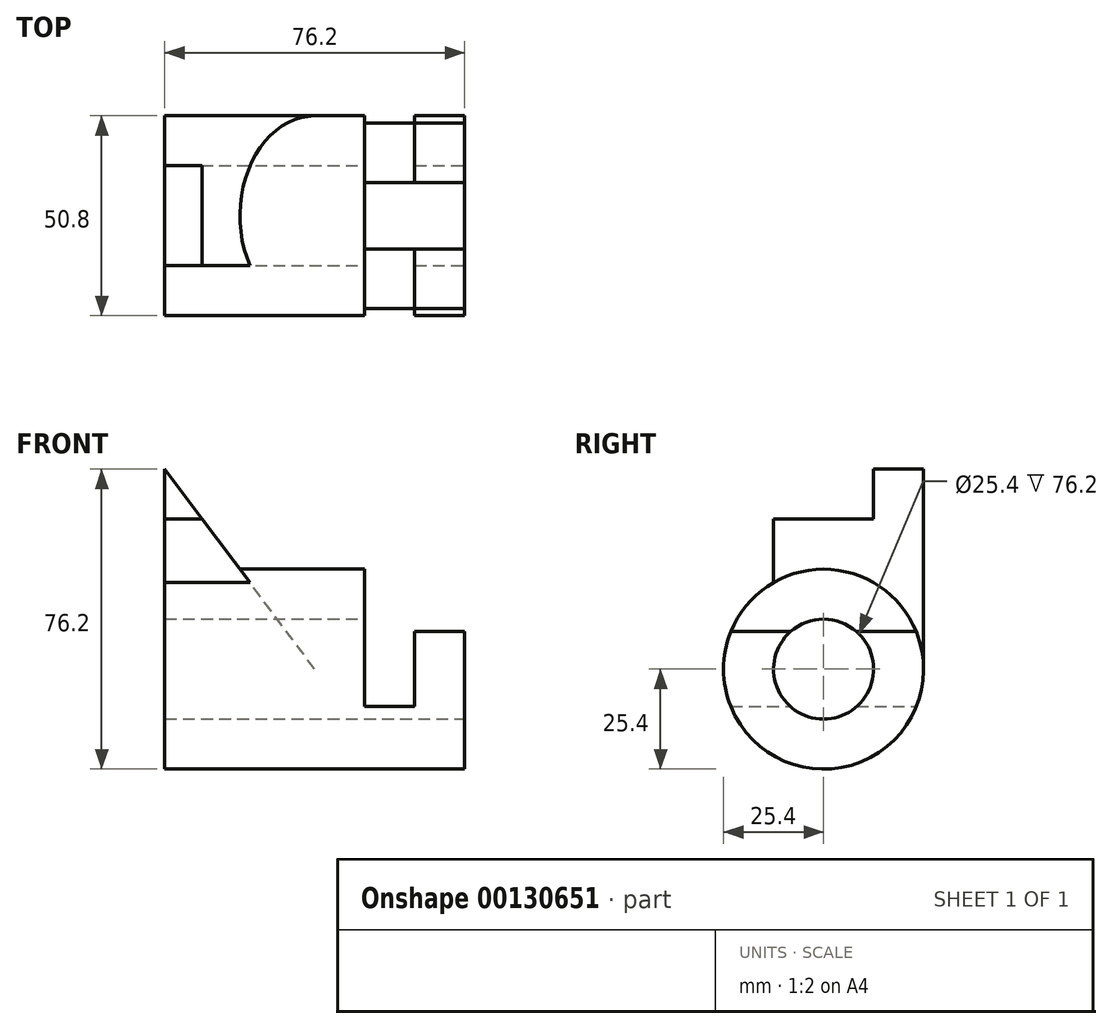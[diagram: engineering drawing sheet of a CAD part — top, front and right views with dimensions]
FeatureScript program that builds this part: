
annotation { "Feature Type Name" : "Feature", "Feature Type Description" : "" }
export const myFeature = defineFeature(function(context is Context, id is Id, definition is map)
    precondition{}
    {
        {
            var Q0;
            Q0=qCreatedBy(makeId("Front.planeOp"),FACE);
            var sketch = newSketch(context, id + "F0", { "sketchPlane" : qUnion([Q0])});
            skLineSegment(sketch, "E0", {"start": v(0, 0) * mm, "end": v(76.2, 0) * mm});
            skLineSegment(sketch, "E1", {"start": v(76.2, 0) * mm, "end": v(76.2, 34.93) * mm});
            skLineSegment(sketch, "E2", {"start": v(76.2, 34.93) * mm, "end": v(63.5, 34.93) * mm});
            skLineSegment(sketch, "E3", {"start": v(63.5, 34.93) * mm, "end": v(63.5, 15.88) * mm});
            skLineSegment(sketch, "E4", {"start": v(63.5, 15.88) * mm, "end": v(50.8, 15.88) * mm});
            skLineSegment(sketch, "E5", {"start": v(50.8, 15.88) * mm, "end": v(50.8, 50.8) * mm});
            skLineSegment(sketch, "E6", {"start": v(50.8, 50.8) * mm, "end": v(19.05, 50.8) * mm});
            skLineSegment(sketch, "E7", {"start": v(19.05, 50.8) * mm, "end": v(0, 76.2) * mm});
            skLineSegment(sketch, "E8", {"start": v(0, 76.2) * mm, "end": v(0, 0) * mm});
            skLineSegment(sketch, "E9", {"start": v(19.05, 50.8) * mm, "end": v(21.43, 47.62) * mm});
            skLineSegment(sketch, "E10", {"start": v(21.43, 47.62) * mm, "end": v(0, 47.62) * mm});
            skLineSegment(sketch, "E11", {"start": v(0, 47.62) * mm, "end": v(0, 76.2) * mm});
            skSolve(sketch);
        }
        {
            var Q0;
            Q0=makeQuery(id+"F0.imprint","IMPRINT",FACE,{"disambiguationData":[TD([[makeQuery(id+"F0.imprint","IMPRINT",EDGE,{"derivedFrom":sQuery(id+"F0.wireOp",EDGE,"E0")}),1.0]])]});
            var Q1;
            Q1=makeQuery(id+"F0.imprint","IMPRINT",FACE,{"disambiguationData":[TD([[makeQuery(id+"F0.imprint","IMPRINT",EDGE,{"derivedFrom":sQuery(id+"F0.wireOp",EDGE,"E7")}),1.0]])]});
            extrude(context, id + "F1", {"entities" : qUnion([Q0, Q1]), "endBound" : BoundingType.SYMMETRIC, "depth" : 50.8 * mm});
        }
        {
            var Q0;
            Q0=makeQuery(id+"F1.opExtrude","SWEPT_FACE",FACE,{"disambiguationData":[OSD([sQuery(id+"F0.wireOp",EDGE,"E1")])]});
            var sketch = newSketch(context, id + "F2", { "sketchPlane" : qUnion([Q0])});
            skCircle(sketch, "E12", {"center": v(0, 25.4) * mm, "radius": 25.4 * mm});
            skSolve(sketch);
        }
        {
            var Q0;
            {var subQ0=sQuery(id+"F2.wireOp",EDGE,"E12");var subQ1=sQuery(id+"F0.wireOp",EDGE,"E1");var subQ2=makeQuery(id+"F1.opExtrude","CAP_EDGE",EDGE,{"disambiguationData":[OSD([subQ1])],"isStart":false});var subQ3=makeQuery(id+"F2.imprint","INTERSECT",VERTEX,{"derivedFrom":[subQ2,subQ0]});Q0=makeQuery(id+"F2.imprint","IMPRINT",FACE,{"disambiguationData":[TD([[makeQuery(id+"F2.imprint","IMPRINT",EDGE,{"disambiguationData":[TD([[subQ3,-1.0]])],"derivedFrom":subQ0}),-1.0]])]});}
            var Q1;
            {var subQ0=sQuery(id+"F2.wireOp",EDGE,"E12");var subQ1=sQuery(id+"F0.wireOp",EDGE,"E1");var subQ2=makeQuery(id+"F1.opExtrude","CAP_EDGE",EDGE,{"disambiguationData":[OSD([subQ1])],"isStart":true});var subQ3=makeQuery(id+"F2.imprint","INTERSECT",VERTEX,{"derivedFrom":[subQ2,subQ0]});Q1=makeQuery(id+"F2.imprint","IMPRINT",FACE,{"disambiguationData":[TD([[makeQuery(id+"F2.imprint","IMPRINT",EDGE,{"disambiguationData":[TD([[subQ3,1.0]])],"derivedFrom":subQ0}),-1.0]])]});}
            extrude(context, id + "F3", {"entities" : qUnion([Q0, Q1]), "operationType" : NewBodyOperationType.REMOVE, "endBound" : BoundingType.THROUGH_ALL, "oppositeDirection" : true, "depth" : 25.4 * mm});
        }
        {
            var Q0;
            Q0=qCreatedBy(makeId("Right.planeOp"),FACE);
            var sketch = newSketch(context, id + "F4", { "sketchPlane" : qUnion([Q0])});
            skLineSegment(sketch, "E13", {"start": v(12.7, 76.2) * mm, "end": v(12.7, 63.5) * mm});
            skLineSegment(sketch, "E14", {"start": v(12.7, 63.5) * mm, "end": v(-12.7, 63.5) * mm});
            skLineSegment(sketch, "E15", {"start": v(-12.7, 63.5) * mm, "end": v(-12.7, 47.4) * mm});
            skArc(sketch, "E16", {"start": v(-12.7, 47.4) * mm, "mid": v(-22, 38.1) * mm, "end": v(-25.4, 25.4) * mm});
            skLineSegment(sketch, "E17", {"start": v(-25.4, 25.4) * mm, "end": v(-25.4, 76.2) * mm});
            skLineSegment(sketch, "E18", {"start": v(-25.4, 76.2) * mm, "end": v(12.7, 76.2) * mm});
            skSolve(sketch);
        }
        {
            var Q0;
            Q0=makeQuery(id+"F4.imprint","IMPRINT",FACE,{"disambiguationData":[TD([[makeQuery(id+"F4.imprint","IMPRINT",EDGE,{"derivedFrom":sQuery(id+"F4.wireOp",EDGE,"E13")}),-1.0]])]});
            extrude(context, id + "F5", {"entities" : qUnion([Q0]), "operationType" : NewBodyOperationType.REMOVE, "endBound" : BoundingType.THROUGH_ALL, "depth" : 25.4 * mm});
        }
        {
            var Q0;
            Q0=makeQuery(id+"F1.opExtrude","SWEPT_FACE",FACE,{"disambiguationData":[OSD([sQuery(id+"F0.wireOp",EDGE,"E5")])]});
            var sketch = newSketch(context, id + "F6", { "sketchPlane" : qUnion([Q0])});
            skLineSegment(sketch, "E19.0", {"start": v(25.4, 25.4) * mm, "end": v(25.4, 50.8) * mm});
            skLineSegment(sketch, "E20.0", {"start": v(-12.7, 50.8) * mm, "end": v(25.4, 50.8) * mm});
            skLineSegment(sketch, "E21.0", {"start": v(-12.7, 50.8) * mm, "end": v(-12.7, 47.4) * mm});
            skArc(sketch, "E22", {"start": v(25.4, 25.4) * mm, "mid": v(12.7, 47.4) * mm, "end": v(-12.7, 47.4) * mm});
            skSolve(sketch);
        }
        {
            var Q0;
            Q0 = qSketchRegion(id + "F6", true);
            extrude(context, id + "F7", {"entities" : qUnion([Q0]), "operationType" : NewBodyOperationType.REMOVE, "oppositeDirection" : true, "depth" : 31.75 * mm});
        }
        {
            var Q0;
            {var subQ0=sQuery(id+"F0.wireOp",EDGE,"E11");var subQ1=sQuery(id+"F0.wireOp",EDGE,"E8");var subQ2=sQuery(id+"F0.wireOp",EDGE,"E7");var subQ3=sQuery(id+"F0.wireOp",EDGE,"E6");var subQ4=sQuery(id+"F0.wireOp",EDGE,"E5");var subQ6=sQuery(id+"F0.wireOp",EDGE,"E1");var subQ7=sQuery(id+"F0.wireOp",EDGE,"E0");Q0=makeQuery(id+"F3.boolean.opBoolean","SPLIT",FACE,{"disambiguationData":[TD([makeQuery(id+"F1.opExtrude","SWEPT_FACE",FACE,{"disambiguationData":[OSD([subQ4])]})])],"derivedFrom":makeQuery(id+"F1.opExtrude","CAP_FACE",FACE,{"disambiguationData":[OSD([subQ7,subQ6,sQuery(id+"F0.wireOp",EDGE,"E2"),sQuery(id+"F0.wireOp",EDGE,"E3"),sQuery(id+"F0.wireOp",EDGE,"E4"),subQ4,subQ3,subQ2,subQ1,subQ0])],"isStart":true})});}
            var sketch = newSketch(context, id + "F8", { "sketchPlane" : qUnion([Q0])});
            skLineSegment(sketch, "E23", {"start": v(-19.05, 25.4) * mm, "end": v(-19.05, 50.8) * mm});
            skLineSegment(sketch, "E24", {"start": v(-19.05, 50.8) * mm, "end": v(-38.1, 25.4) * mm});
            skLineSegment(sketch, "E25", {"start": v(-38.1, 25.4) * mm, "end": v(-19.05, 25.4) * mm});
            skSolve(sketch);
        }
        {
            var Q0;
            Q0 = qSketchRegion(id + "F8", true);
            extrude(context, id + "F9", {"entities" : qUnion([Q0]), "operationType" : NewBodyOperationType.ADD, "endBound" : BoundingType.UP_TO_NEXT, "oppositeDirection" : true, "depth" : 8 * mm});
        }
        {
            var Q0;
            {var subQ0=sQuery(id+"F2.wireOp",EDGE,"E12");var subQ1=sQuery(id+"F0.wireOp",EDGE,"E1");var subQ2=makeQuery(id+"F2.imprint","INTERSECT",VERTEX,{"derivedFrom":[makeQuery(id+"F1.opExtrude","CAP_EDGE",EDGE,{"disambiguationData":[OSD([subQ1])],"isStart":true}),subQ0]});Q0=makeQuery(id+"F2.imprint","IMPRINT",FACE,{"disambiguationData":[TD([[makeQuery(id+"F2.imprint","IMPRINT",EDGE,{"disambiguationData":[TD([[subQ2,-1.0]])],"derivedFrom":subQ0}),1.0]])]});}
            var sketch = newSketch(context, id + "F10", { "sketchPlane" : qUnion([Q0])});
            skCircle(sketch, "E26", {"center": v(0, 25.4) * mm, "radius": 12.7 * mm});
            skSolve(sketch);
        }
        {
            var Q0;
            Q0 = qSketchRegion(id + "F10", true);
            extrude(context, id + "F11", {"entities" : qUnion([Q0]), "operationType" : NewBodyOperationType.REMOVE, "endBound" : BoundingType.THROUGH_ALL, "oppositeDirection" : true, "depth" : 25.4 * mm});
        }
        {
            var Q0;
            Q0=makeQuery(id+"F1.opExtrude","SWEPT_FACE",FACE,{"disambiguationData":[OSD([sQuery(id+"F0.wireOp",EDGE,"E1")])]});
            var sketch = newSketch(context, id + "F12", { "sketchPlane" : qUnion([Q0])});
            skArc(sketch, "E27", {"start": v(25.4, 25.4) * mm, "mid": v(24.93, 30.25) * mm, "end": v(23.55, 34.92) * mm});
            skLineSegment(sketch, "E28", {"start": v(23.55, 34.93) * mm, "end": v(25.4, 34.93) * mm});
            skLineSegment(sketch, "E29", {"start": v(25.4, 34.93) * mm, "end": v(25.4, 25.4) * mm});
            skSolve(sketch);
        }
        {
            var Q0;
            Q0 = qSketchRegion(id + "F12", true);
            extrude(context, id + "F13", {"entities" : qUnion([Q0]), "operationType" : NewBodyOperationType.REMOVE, "oppositeDirection" : true, "depth" : 12.7 * mm});
        }
        {
            var Q0;
            Q0=makeQuery(id+"F5.boolean.opBoolean","COPY",FACE,{"derivedFrom":makeQuery(id+"F5.opExtrude","SWEPT_FACE",FACE,{"disambiguationData":[OSD([sQuery(id+"F4.wireOp",EDGE,"E15")])]})});
            var sketch = newSketch(context, id + "F14", { "sketchPlane" : qUnion([Q0])});
            skLineSegment(sketch, "E30", {"start": v(0, 47.4) * mm, "end": v(21.6, 47.4) * mm});
            skLineSegment(sketch, "E31", {"start": v(21.6, 47.4) * mm, "end": v(9.52, 63.5) * mm});
            skLineSegment(sketch, "E32", {"start": v(9.52, 63.5) * mm, "end": v(0, 63.5) * mm});
            skLineSegment(sketch, "E33", {"start": v(0, 63.5) * mm, "end": v(0, 47.4) * mm});
            skSolve(sketch);
        }
        {
            var Q0;
            Q0 = qSketchRegion(id + "F14", true);
            extrude(context, id + "F15", {"entities" : qUnion([Q0]), "operationType" : NewBodyOperationType.ADD, "oppositeDirection" : true, "depth" : 12.7 * mm});
        }
    });
